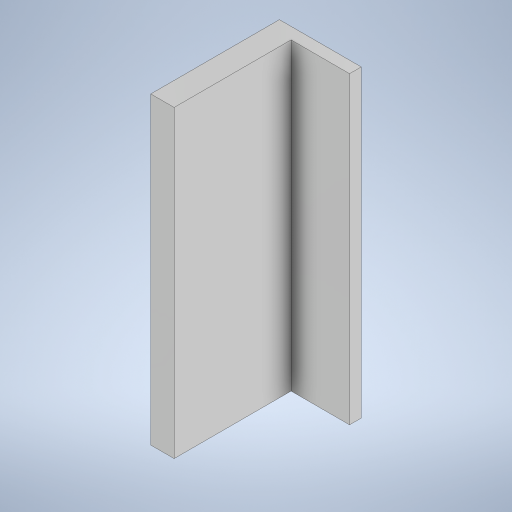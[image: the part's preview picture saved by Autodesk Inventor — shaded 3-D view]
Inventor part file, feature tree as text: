
AUTODESK INVENTOR PART (.ipt)
format: ipt  version: 2024 (Build 280153000, 153)  size: 247,808 bytes
history: native  units: mm
features: extrude x4, sketch x4, chamfer x1
ambient origin geometry x8: Origin, YZ Plane, XZ Plane, XY Plane, X Axis, Y Axis, Z Axis, Center Point
bodies: Solid1 (feature_tree)
feature tree (9):
  extrude  "Extrusion1"  Depth=20.0mm
  chamfer  "Chamfer1"  Distance=260.0mm
  extrude  "Extrusion2"  Depth=10.0mm
  extrude  "Extrusion4"  Depth=50.0mm TaperAngle=0.0deg
  extrude  "Extrusion5"  Depth=50.0mm TaperAngle=0.0deg
  sketch  "Sketch1"  dims[d0=110.0mm d1=20.0mm]
  sketch  "Sketch2"  dims[d3=60.0mm d4=260.0mm d5=0.0mm]
  sketch  "Sketch4"  dims[d6=100.0mm d7=2.0mm d8=45.0deg d9=10.0mm]
  sketch  "Sketch5"  dims[d10=50.0mm d11=0.0mm d18=82.0mm d19=0.0mm d20=82.0mm d21=0.0mm]
